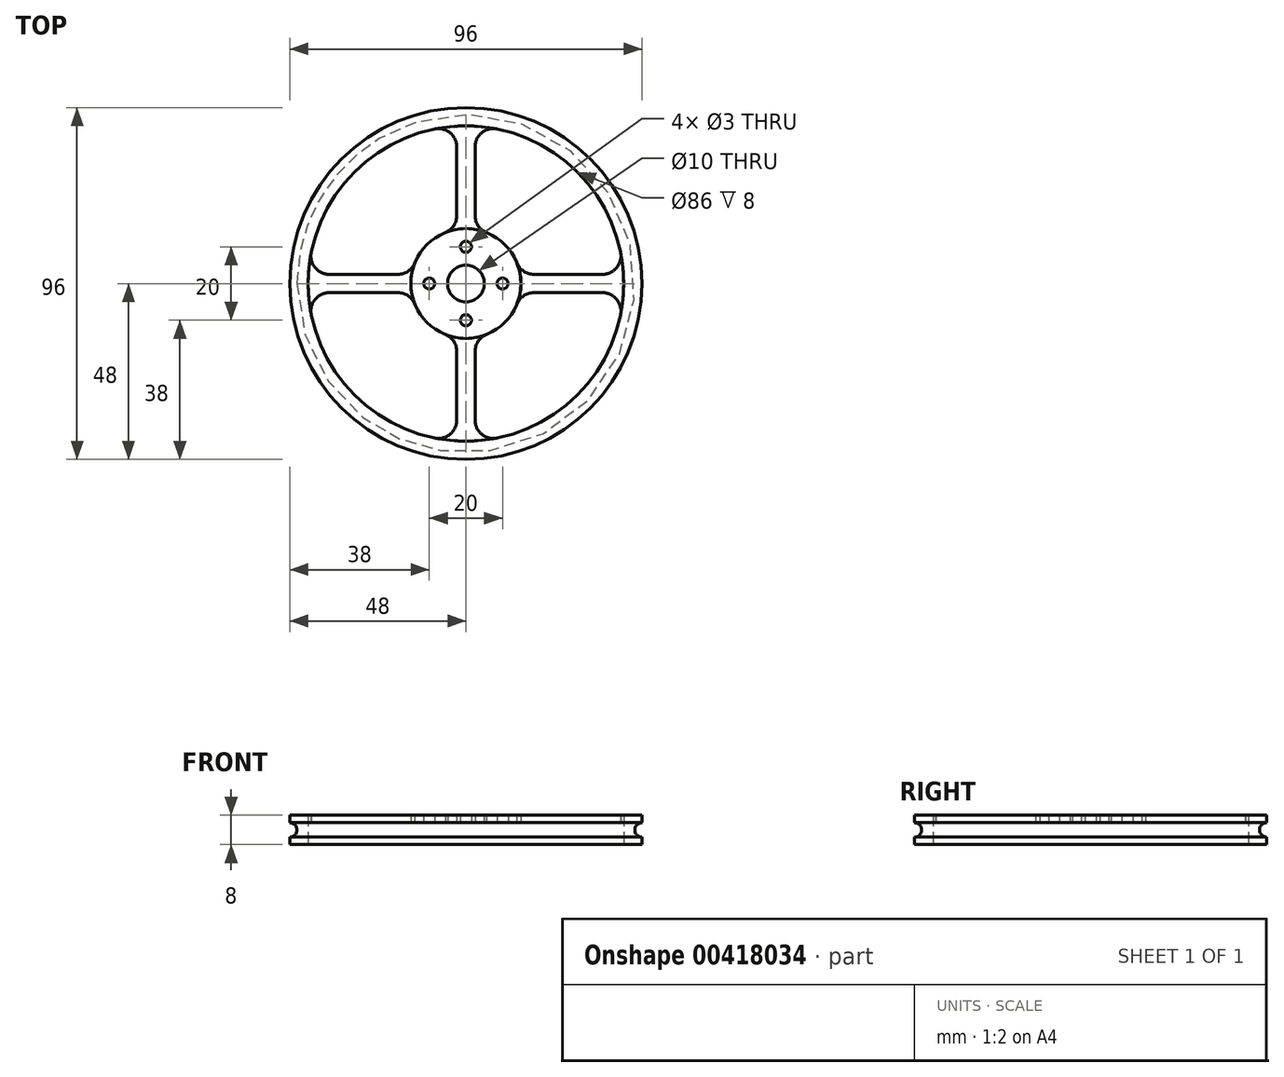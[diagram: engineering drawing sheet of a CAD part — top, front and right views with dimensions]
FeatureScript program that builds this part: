
annotation { "Feature Type Name" : "Feature", "Feature Type Description" : "" }
export const myFeature = defineFeature(function(context is Context, id is Id, definition is map)
    precondition{}
    {
        {
            var Q0;
            Q0=qCreatedBy(makeId("Top.planeOp"),FACE);
            var sketch = newSketch(context, id + "F0", { "sketchPlane" : qUnion([Q0])});
            skArc(sketch, "E0", {"start": v(5.63, -13.9) * mm, "mid": v(10.6, -10.6) * mm, "end": v(13.9, -5.62) * mm});
            skLineSegment(sketch, "E1", {"start": v(0, 0) * mm, "end": v(10, 0) * mm, "construction": true});
            skLineSegment(sketch, "E2", {"start": v(0, 0) * mm, "end": v(0, 10) * mm, "construction": true});
            skCircle(sketch, "E3", {"center": v(0, 0) * mm, "radius": 5 * mm});
            skCircle(sketch, "E4", {"center": v(0, 10) * mm, "radius": 1.5 * mm});
            skCircle(sketch, "E5", {"center": v(10, 0) * mm, "radius": 1.5 * mm});
            skCircle(sketch, "E6.MirrorC", {"center": v(-10, 0) * mm, "radius": 1.5 * mm});
            skCircle(sketch, "E7.MirrorC", {"center": v(0, -10) * mm, "radius": 1.5 * mm});
            skCircle(sketch, "E8", {"center": v(0, 0) * mm, "radius": 48 * mm});
            skArc(sketch, "E9.0", {"start": v(-42.15, -8.49) * mm, "mid": v(-30.4, -30.4) * mm, "end": v(-8.49, -42.15) * mm});
            skLineSegment(sketch, "E10", {"start": v(0, -15) * mm, "end": v(0, -43) * mm});
            skLineSegment(sketch, "E11.0", {"start": v(-2.5, -18.54) * mm, "end": v(-2.5, -37.25) * mm});
            skLineSegment(sketch, "E12.MirrorCS", {"start": v(2.5, -18.54) * mm, "end": v(2.5, -37.25) * mm});
            skLineSegment(sketch, "E13.MirrorCS", {"start": v(2.5, 18.54) * mm, "end": v(2.5, 37.25) * mm});
            skLineSegment(sketch, "E14.MirrorCS", {"start": v(-2.5, 18.54) * mm, "end": v(-2.5, 37.25) * mm});
            skLineSegment(sketch, "E15", {"start": v(15, 0) * mm, "end": v(43, 0) * mm});
            skLineSegment(sketch, "E16.0", {"start": v(18.54, -2.5) * mm, "end": v(37.25, -2.5) * mm});
            skLineSegment(sketch, "E17.MirrorCS", {"start": v(18.54, 2.5) * mm, "end": v(37.25, 2.5) * mm});
            skLineSegment(sketch, "E18.MirrorCS", {"start": v(-18.54, 2.5) * mm, "end": v(-37.25, 2.5) * mm});
            skLineSegment(sketch, "E19.MirrorCS", {"start": v(-18.54, -2.5) * mm, "end": v(-37.25, -2.5) * mm});
            skArc(sketch, "E20.trimOffspring", {"start": v(13.9, 5.62) * mm, "mid": v(10.6, 10.6) * mm, "end": v(5.62, 13.9) * mm});
            skArc(sketch, "E21.trimOffspring", {"start": v(-5.63, 13.9) * mm, "mid": v(-10.6, 10.6) * mm, "end": v(-13.9, 5.63) * mm});
            skArc(sketch, "E22.trimOffspring", {"start": v(-13.9, -5.62) * mm, "mid": v(-10.6, -10.6) * mm, "end": v(-5.63, -13.9) * mm});
            skPoint(sketch, "E23.visualSharp", {"position": v(-14.8, 2.5) * mm});
            skArc(sketch, "E23.filletArc", {"start": v(-18.54, 2.5) * mm, "mid": v(-15.75, 3.35) * mm, "end": v(-13.9, 5.62) * mm});
            skPoint(sketch, "E24.visualSharp", {"position": v(-2.5, 14.8) * mm});
            skArc(sketch, "E24.filletArc", {"start": v(-5.63, 13.9) * mm, "mid": v(-3.35, 15.75) * mm, "end": v(-2.5, 18.54) * mm});
            skPoint(sketch, "E25.visualSharp", {"position": v(2.5, 14.8) * mm});
            skArc(sketch, "E25.filletArc", {"start": v(2.5, 18.54) * mm, "mid": v(3.35, 15.75) * mm, "end": v(5.63, 13.9) * mm});
            skPoint(sketch, "E26.visualSharp", {"position": v(14.8, 2.5) * mm});
            skArc(sketch, "E26.filletArc", {"start": v(13.9, 5.62) * mm, "mid": v(15.75, 3.35) * mm, "end": v(18.54, 2.5) * mm});
            skPoint(sketch, "E27.visualSharp", {"position": v(14.8, -2.5) * mm});
            skArc(sketch, "E27.filletArc", {"start": v(18.54, -2.5) * mm, "mid": v(15.75, -3.35) * mm, "end": v(13.9, -5.62) * mm});
            skPoint(sketch, "E28.visualSharp", {"position": v(2.5, -14.8) * mm});
            skArc(sketch, "E28.filletArc", {"start": v(5.62, -13.9) * mm, "mid": v(3.35, -15.75) * mm, "end": v(2.5, -18.54) * mm});
            skPoint(sketch, "E29.visualSharp", {"position": v(-14.8, -2.5) * mm});
            skArc(sketch, "E29.filletArc", {"start": v(-13.9, -5.62) * mm, "mid": v(-15.75, -3.35) * mm, "end": v(-18.54, -2.5) * mm});
            skPoint(sketch, "E30.visualSharp", {"position": v(-2.5, -14.8) * mm});
            skArc(sketch, "E30.filletArc", {"start": v(-2.5, -18.54) * mm, "mid": v(-3.35, -15.75) * mm, "end": v(-5.63, -13.9) * mm});
            skArc(sketch, "E31.trimOffspring", {"start": v(-8.49, 42.15) * mm, "mid": v(-30.4, 30.4) * mm, "end": v(-42.15, 8.49) * mm});
            skArc(sketch, "E32.trimOffspring", {"start": v(42.15, 8.49) * mm, "mid": v(30.4, 30.4) * mm, "end": v(8.49, 42.15) * mm});
            skArc(sketch, "E33.trimOffspring", {"start": v(8.49, -42.15) * mm, "mid": v(30.4, -30.4) * mm, "end": v(42.15, -8.49) * mm});
            skPoint(sketch, "E34.visualSharp", {"position": v(-42.93, -2.5) * mm});
            skArc(sketch, "E34.filletArc", {"start": v(-37.25, -2.5) * mm, "mid": v(-41.12, -4.33) * mm, "end": v(-42.15, -8.49) * mm});
            skPoint(sketch, "E35.newPointA", {"position": v(-2.5, -38) * mm});
            skArc(sketch, "E35.filletArc", {"start": v(-8.49, -42.15) * mm, "mid": v(-4.33, -41.12) * mm, "end": v(-2.5, -37.25) * mm});
            skPoint(sketch, "E36.newPointA", {"position": v(2.5, -38) * mm});
            skArc(sketch, "E36.filletArc", {"start": v(2.5, -37.25) * mm, "mid": v(4.33, -41.12) * mm, "end": v(8.49, -42.15) * mm});
            skPoint(sketch, "E37.visualSharp", {"position": v(42.93, -2.5) * mm});
            skArc(sketch, "E37.filletArc", {"start": v(42.15, -8.49) * mm, "mid": v(41.12, -4.33) * mm, "end": v(37.25, -2.5) * mm});
            skPoint(sketch, "E38.visualSharp", {"position": v(42.93, 2.5) * mm});
            skArc(sketch, "E38.filletArc", {"start": v(37.25, 2.5) * mm, "mid": v(41.12, 4.33) * mm, "end": v(42.15, 8.49) * mm});
            skPoint(sketch, "E39.newPointA", {"position": v(-2.5, 38) * mm});
            skArc(sketch, "E39.filletArc", {"start": v(-2.5, 37.25) * mm, "mid": v(-4.33, 41.12) * mm, "end": v(-8.49, 42.15) * mm});
            skPoint(sketch, "E40.newPointB", {"position": v(2.5, 38) * mm});
            skArc(sketch, "E40.filletArc", {"start": v(8.49, 42.15) * mm, "mid": v(4.33, 41.12) * mm, "end": v(2.5, 37.25) * mm});
            skPoint(sketch, "E41.visualSharp", {"position": v(-42.93, 2.5) * mm});
            skArc(sketch, "E41.filletArc", {"start": v(-42.15, 8.49) * mm, "mid": v(-41.12, 4.33) * mm, "end": v(-37.25, 2.5) * mm});
            skCircle(sketch, "E42", {"center": v(0, 0) * mm, "radius": 15 * mm});
            skCircle(sketch, "E43", {"center": v(0, 0) * mm, "radius": 43 * mm});
            skSolve(sketch);
        }
        {
            var Q0;
            Q0=makeQuery(id+"F0.imprint","IMPRINT",FACE,{"disambiguationData":[TD([[makeQuery(id+"F0.imprint","IMPRINT",EDGE,{"derivedFrom":sQuery(id+"F0.wireOp",EDGE,"E8")}),1.0]])]});
            extrude(context, id + "F1", {"entities" : qUnion([Q0]), "depth" : 1 * mm, "hasSecondDirection" : true, "secondDirectionOppositeDirection" : true, "secondDirectionDepth" : 7 * mm});
        }
        {
            var Q0;
            Q0=makeQuery(id+"F0.imprint","IMPRINT",FACE,{"disambiguationData":[TD([[makeQuery(id+"F0.imprint","IMPRINT",EDGE,{"derivedFrom":sQuery(id+"F0.wireOp",EDGE,"E3")}),-1.0]])]});
            extrude(context, id + "F2", {"entities" : qUnion([Q0]), "endBound" : BoundingType.SYMMETRIC, "depth" : 2 * mm});
        }
        {
            var Q0;
            {var subQ2=sQuery(id+"F0.wireOp",EDGE,"E10");Q0=makeQuery(id+"F0.imprint","IMPRINT",FACE,{"disambiguationData":[TD([[makeQuery(id+"F0.imprint","IMPRINT",EDGE,{"derivedFrom":subQ2}),-1.0]])]});}
            var Q1;
            {var subQ2=sQuery(id+"F0.wireOp",EDGE,"E10");Q1=makeQuery(id+"F0.imprint","IMPRINT",FACE,{"disambiguationData":[TD([[makeQuery(id+"F0.imprint","IMPRINT",EDGE,{"derivedFrom":subQ2}),1.0]])]});}
            var Q2;
            {var subQ2=sQuery(id+"F0.wireOp",EDGE,"E15");Q2=makeQuery(id+"F0.imprint","IMPRINT",FACE,{"disambiguationData":[TD([[makeQuery(id+"F0.imprint","IMPRINT",EDGE,{"derivedFrom":subQ2}),-1.0]])]});}
            var Q3;
            {var subQ2=sQuery(id+"F0.wireOp",EDGE,"E15");Q3=makeQuery(id+"F0.imprint","IMPRINT",FACE,{"disambiguationData":[TD([[makeQuery(id+"F0.imprint","IMPRINT",EDGE,{"derivedFrom":subQ2}),1.0]])]});}
            var Q4;
            Q4=makeQuery(id+"F0.imprint","IMPRINT",FACE,{"disambiguationData":[TD([[makeQuery(id+"F0.imprint","IMPRINT",EDGE,{"derivedFrom":sQuery(id+"F0.wireOp",EDGE,"E13.MirrorCS")}),1.0]])]});
            var Q5;
            Q5=makeQuery(id+"F0.imprint","IMPRINT",FACE,{"disambiguationData":[TD([[makeQuery(id+"F0.imprint","IMPRINT",EDGE,{"derivedFrom":sQuery(id+"F0.wireOp",EDGE,"E18.MirrorCS")}),1.0]])]});
            extrude(context, id + "F3", {"entities" : qUnion([Q0, Q1, Q2, Q3, Q4, Q5]), "endBound" : BoundingType.SYMMETRIC, "depth" : 2 * mm});
        }
        {
            var Q0;
            Q0=qCreatedBy(makeId("Right.planeOp"),FACE);
            var sketch = newSketch(context, id + "F4", { "sketchPlane" : qUnion([Q0])});
            skLineSegment(sketch, "E44", {"start": v(-48, -7) * mm, "end": v(-48, 1) * mm});
            skLineSegment(sketch, "E45", {"start": v(48, 1) * mm, "end": v(48, -7) * mm});
            skCircle(sketch, "E46", {"center": v(48, -3) * mm, "radius": 1.95 * mm});
            skLineSegment(sketch, "E47", {"start": v(0, 23.23) * mm, "end": v(0, -30.58) * mm});
            skSolve(sketch);
        }
        {
            var Q0;
            {var subQ0=sQuery(id+"F4.wireOp",EDGE,"E46");var subQ1=sQuery(id+"F4.wireOp",EDGE,"E45");var subQ2=makeQuery(id+"F4.imprint","INTERSECT",VERTEX,{"disambiguationData":[OD(0.0)],"derivedFrom":[subQ1,subQ0]});Q0=makeQuery(id+"F4.imprint","IMPRINT",FACE,{"disambiguationData":[TD([[makeQuery(id+"F4.imprint","IMPRINT",EDGE,{"disambiguationData":[TD([[subQ2,1.0]])],"derivedFrom":subQ1}),-1.0]])]});}
            var Q1;
            Q1=sQuery(id+"F4.wireOp",EDGE,"E46");
            var Q2;
            Q2=sQuery(id+"F4.wireOp",EDGE,"E47");
            revolve(context, id + "F5", {"operationType" : NewBodyOperationType.REMOVE, "entities" : qUnion([Q0]), "surfaceEntities" : qUnion([Q1]), "axis" : qUnion([Q2]), "revolveType" : RevolveType.FULL, "oppositeDirection" : true});
        }
    });
